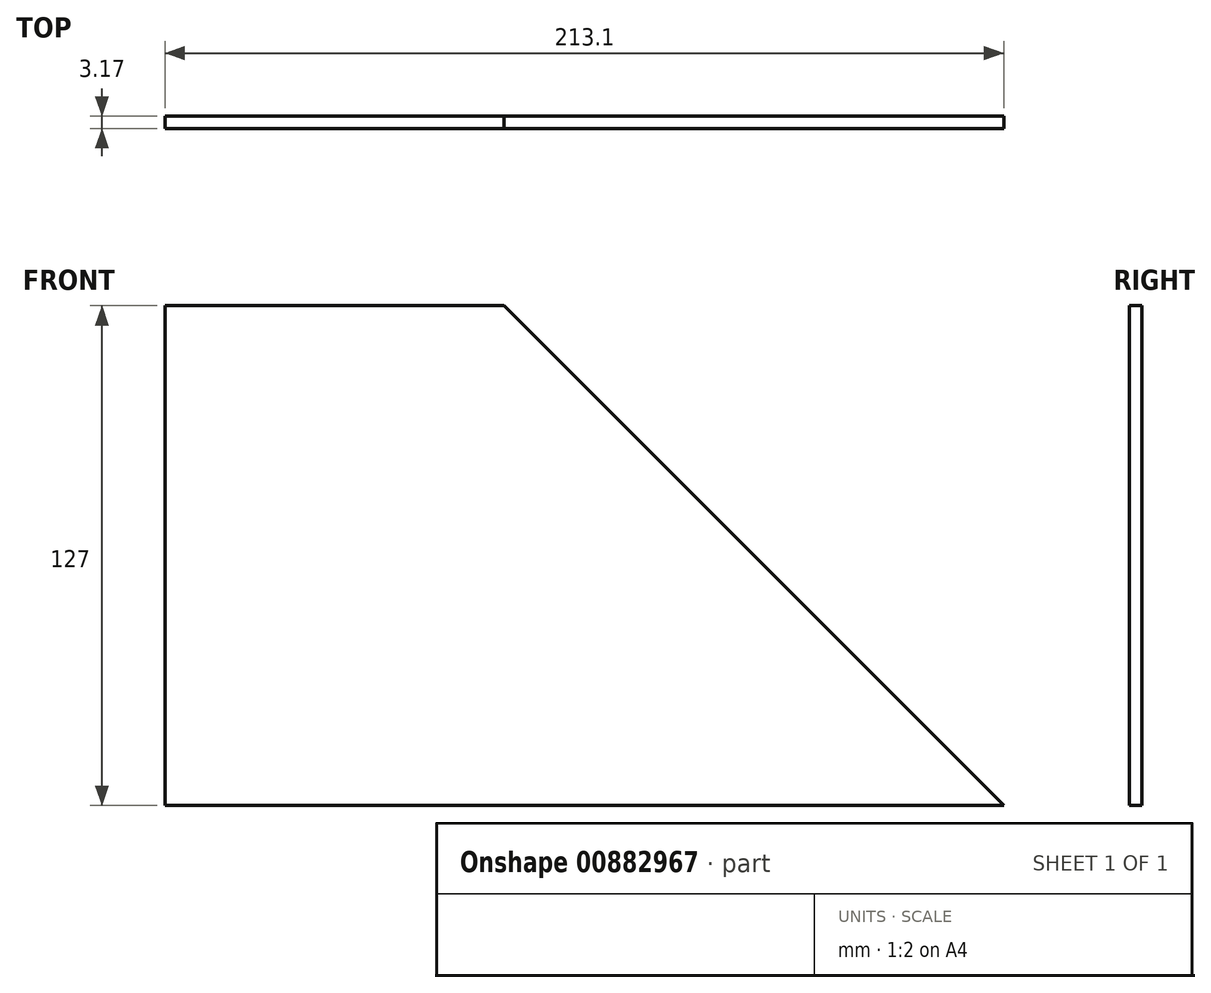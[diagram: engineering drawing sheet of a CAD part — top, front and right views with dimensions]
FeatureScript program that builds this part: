
annotation { "Feature Type Name" : "Feature", "Feature Type Description" : "" }
export const myFeature = defineFeature(function(context is Context, id is Id, definition is map)
    precondition{}
    {
        {
            var Q0;
            Q0=qCreatedBy(makeId("Front.planeOp"),FACE);
            var sketch = newSketch(context, id + "F0", { "sketchPlane" : qUnion([Q0])});
            skLineSegment(sketch, "E0", {"start": v(0, 0) * mm, "end": v(0, 127) * mm});
            skLineSegment(sketch, "E1", {"start": v(0, 127) * mm, "end": v(86.1, 127) * mm});
            skLineSegment(sketch, "E2", {"start": v(86.1, 127) * mm, "end": v(213.1, 0) * mm});
            skLineSegment(sketch, "E3", {"start": v(213.1, 0) * mm, "end": v(0, 0) * mm});
            skSolve(sketch);
        }
        {
            var Q0;
            Q0 = qSketchRegion(id + "F0", true);
            extrude(context, id + "F1", {"entities" : qUnion([Q0]), "depth" : 3.17 * mm, "offsetDistance" : 25.4 * mm});
        }
    });
